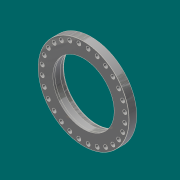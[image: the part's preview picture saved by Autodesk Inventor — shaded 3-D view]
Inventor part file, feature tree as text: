
AUTODESK INVENTOR PART (.ipt)
format: ipt  version: 2017.3 (Build 213256000, 256)  size: 395,264 bytes
history: native  units: in
note: dims shown in document units (in); Inventor stores cm internally (conversion verified against a paired STEP export)
features: sketch x6, extrude x4, chamfer x4, fillet x2, hole x1, pattern_circular x1, revolve x1, projected_geometry x1
ambient origin geometry x8: Origin, YZ Plane, XZ Plane, XY Plane, X Axis, Y Axis, Z Axis, Center Point
bodies: Solid1 (feature_tree)
feature tree (20):
  extrude  "Extrusion1"  Depth=29.0in
  extrude  "Extrusion2"  Depth=33.75in
  extrude  "Extrusion3"  Depth=34.75in
  extrude  "Extrusion9"  Depth=19.625in
  hole  "Hole1"  [1 undecoded]
  chamfer  "Chamfer3"  Distance=0.125in
  pattern_circular  "Circular Pattern1"  [2 undecoded]
  chamfer  "Chamfer2"  Distance=0.0312in Angle=45.0deg
  fillet  "Fillet2"  Radius=0.125in
  chamfer  "Chamfer4"  Distance=32.0in
  revolve  "Revolution3"  [1 undecoded]
  fillet  "Fillet7"  Radius=0.125in
  chamfer  "Chamfer8"  Distance=0.25in
  sketch  "Sketch1"  dims[d0=43.0in d1=29.0in]
  sketch  "Sketch2"  dims[d2=3.625in d3=0.0in d4=33.75in]
  sketch  "Sketch3"  dims[d5=0.0625in d6=0.0in d7=34.75in]
  sketch  "Sketch4"  dims[d8=2.4375in d9=0.0in d13=19.625in]
  sketch  "Sketch12"  dims[d14=0.0442in]
  sketch  "Sketch15"  dims[d15=1.875in d16=0.75in d17=0.375in d18=0.25in d19=0.5635in d20=1.0in d21=0.8108in d22=11.0236in d23=360.0deg d25=0.0625in d26=0.125in d27=0.0687in d29=0.4375in d30=0.0312in d31=0.125in d32=45.0deg d33=0.0625in d34=0.125in d35=45.0deg d98=32.0in d99=0.3125in d100=0.125in d101=0.25in d102=0.2577in d103=0.5in d104=0.875in d105=0.3852in d106=29.375in d108=90.0deg d109=0.0312in d110=0.0312in d111=0.125in d112=45.0deg d120=1.0in d129=1.0in d130=0.0in d134=0.0625in d135=0.1374in]
  projected_geometry  "Projected Loop1"
note: 4 required parameter values undecoded (feature->parameter linkage not recoverable at this tier; creation-order binding heuristic only, values carry confidence <= 0.55)